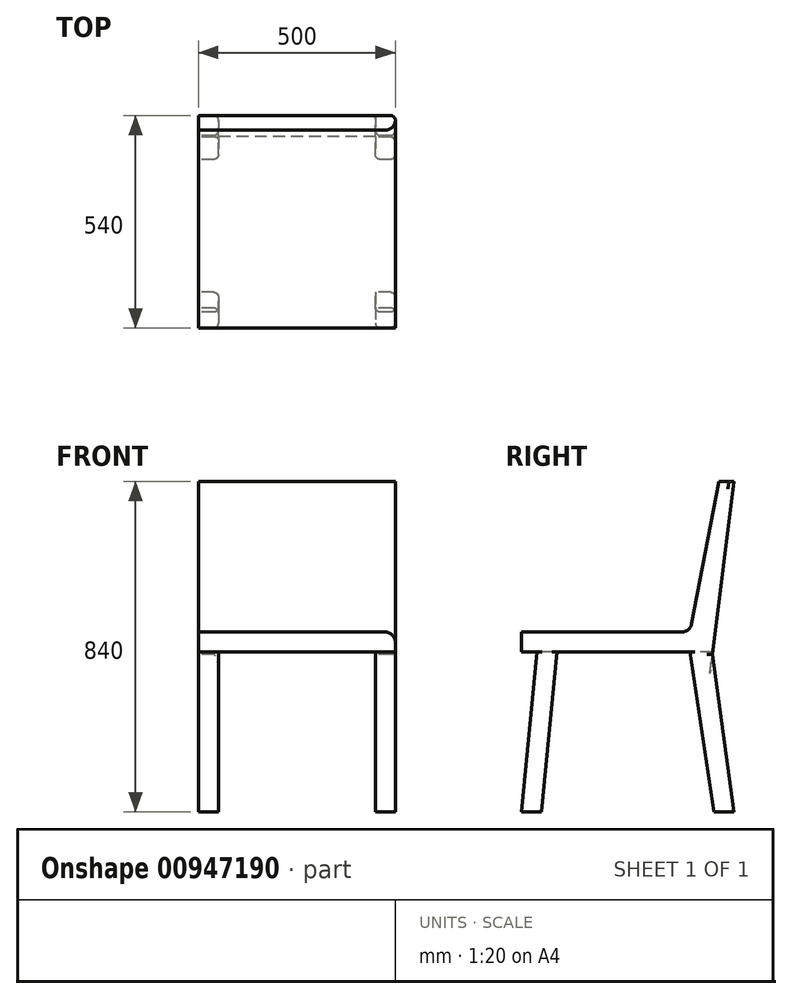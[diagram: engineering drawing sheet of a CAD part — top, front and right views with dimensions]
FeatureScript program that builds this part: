
annotation { "Feature Type Name" : "Feature", "Feature Type Description" : "" }
export const myFeature = defineFeature(function(context is Context, id is Id, definition is map)
    precondition{}
    {
        {
            var Q0;
            Q0=qCreatedBy(makeId("Top.planeOp"),FACE);
            var sketch = newSketch(context, id + "F0", { "sketchPlane" : qUnion([Q0])});
            skLineSegment(sketch, "E0.bottom", {"start": v(0, 0) * mm, "end": v(500, 0) * mm});
            skLineSegment(sketch, "E0.top", {"start": v(0, 540) * mm, "end": v(500, 540) * mm});
            skLineSegment(sketch, "E0.left", {"start": v(0, 0) * mm, "end": v(0, 540) * mm});
            skLineSegment(sketch, "E0.right", {"start": v(500, 0) * mm, "end": v(500, 540) * mm});
            skSolve(sketch);
        }
        {
            var Q0;
            Q0=makeQuery(id+"F0.imprint","IMPRINT",FACE,{"disambiguationData":[TD([[makeQuery(id+"F0.imprint","IMPRINT",EDGE,{"derivedFrom":sQuery(id+"F0.wireOp",EDGE,"E0.bottom")}),1.0]])]});
            extrude(context, id + "F1", {"entities" : qUnion([Q0]), "depth" : 840 * mm, "offsetDistance" : 25.4 * mm});
        }
        {
            var Q0;
            Q0=makeQuery(id+"F1.opExtrude","SWEPT_FACE",FACE,{"disambiguationData":[OSD([sQuery(id+"F0.wireOp",EDGE,"E0.bottom")])]});
            var sketch = newSketch(context, id + "F2", { "sketchPlane" : qUnion([Q0])});
            skLineSegment(sketch, "E1.bottom", {"start": v(50.8, 0) * mm, "end": v(449.2, 0) * mm});
            skLineSegment(sketch, "E1.top", {"start": v(50.8, 406.4) * mm, "end": v(449.2, 406.4) * mm});
            skLineSegment(sketch, "E1.left", {"start": v(50.8, 0) * mm, "end": v(50.8, 406.4) * mm});
            skLineSegment(sketch, "E1.right", {"start": v(449.2, 0) * mm, "end": v(449.2, 406.4) * mm});
            skPoint(sketch, "E2.right.end.orphan", {"position": v(500, 420) * mm});
            skSolve(sketch);
        }
        {
            var Q0;
            Q0 = qSketchRegion(id + "F2", true);
            extrude(context, id + "F3", {"entities" : qUnion([Q0]), "operationType" : NewBodyOperationType.REMOVE, "oppositeDirection" : true, "depth" : 820.42 * mm, "offsetDistance" : 25.4 * mm});
        }
        {
            var Q0;
            Q0=makeQuery(id+"F1.opExtrude","SWEPT_FACE",FACE,{"disambiguationData":[OSD([sQuery(id+"F0.wireOp",EDGE,"E0.left")])]});
            var sketch = newSketch(context, id + "F4", { "sketchPlane" : qUnion([Q0])});
            skLineSegment(sketch, "E3", {"start": v(-489.2, 0) * mm, "end": v(-428.28, 406.4) * mm});
            skLineSegment(sketch, "E4", {"start": v(-428.28, 406.4) * mm, "end": v(-90.89, 406.4) * mm});
            skLineSegment(sketch, "E5", {"start": v(-90.89, 406.4) * mm, "end": v(-50.8, 0) * mm});
            skLineSegment(sketch, "E6", {"start": v(-502.68, 840) * mm, "end": v(-428.28, 457.2) * mm});
            skLineSegment(sketch, "E7", {"start": v(-428.28, 457.2) * mm, "end": v(0, 457.2) * mm});
            skPoint(sketch, "E7.endSnap0", {"position": v(0, 420) * mm});
            skLineSegment(sketch, "E8", {"start": v(0, 457.2) * mm, "end": v(0, 840) * mm});
            skLineSegment(sketch, "E9", {"start": v(-489.2, 0) * mm, "end": v(-50.8, 0) * mm});
            skLineSegment(sketch, "E10.bottom", {"start": v(-540, 840) * mm, "end": v(0, 840) * mm});
            skLineSegment(sketch, "E10.top", {"start": v(-540, 0) * mm, "end": v(0, 0) * mm});
            skLineSegment(sketch, "E10.left", {"start": v(-540, 840) * mm, "end": v(-540, 0) * mm});
            skLineSegment(sketch, "E10.right", {"start": v(0, 840) * mm, "end": v(0, 0) * mm});
            skLineSegment(sketch, "E11", {"start": v(0, 0) * mm, "end": v(-40.09, 406.4) * mm});
            skLineSegment(sketch, "E12", {"start": v(-40.09, 406.4) * mm, "end": v(0, 406.4) * mm});
            skLineSegment(sketch, "E13", {"start": v(-540, 0) * mm, "end": v(-485.04, 400.62) * mm});
            skLineSegment(sketch, "E14", {"start": v(-485.04, 400.62) * mm, "end": v(-540, 840) * mm});
            skSolve(sketch);
        }
        {
            var Q0;
            Q0=makeQuery(id+"F4.imprint","IMPRINT",FACE,{"disambiguationData":[TD([[makeQuery(id+"F4.imprint","IMPRINT",EDGE,{"derivedFrom":sQuery(id+"F4.wireOp",EDGE,"E3")}),-1.0]])]});
            var Q1;
            {var subQ0=sQuery(id+"F4.wireOp",EDGE,"E6");Q1=makeQuery(id+"F4.imprint","IMPRINT",FACE,{"disambiguationData":[TD([[makeQuery(id+"F4.imprint","IMPRINT",EDGE,{"derivedFrom":subQ0}),1.0]])]});}
            var Q2;
            Q2=makeQuery(id+"F4.imprint","IMPRINT",FACE,{"disambiguationData":[TD([[makeQuery(id+"F4.imprint","IMPRINT",EDGE,{"derivedFrom":sQuery(id+"F4.wireOp",EDGE,"E10.left")}),1.0]])]});
            var Q3;
            {var subQ0=sQuery(id+"F4.wireOp",EDGE,"E11");Q3=makeQuery(id+"F4.imprint","IMPRINT",FACE,{"disambiguationData":[TD([[makeQuery(id+"F4.imprint","IMPRINT",EDGE,{"derivedFrom":subQ0}),-1.0]])]});}
            extrude(context, id + "F5", {"entities" : qUnion([Q0, Q1, Q2, Q3]), "operationType" : NewBodyOperationType.REMOVE, "oppositeDirection" : true, "depth" : 772.16 * mm, "offsetDistance" : 25.4 * mm});
        }
        {
            var Q0;
            Q0=makeQuery(id+"F5.boolean.opBoolean","COPY",EDGE,{"derivedFrom":makeQuery(id+"F5.opExtrude","SWEPT_EDGE",EDGE,{"disambiguationData":[OSD([sQuery(id+"F4.wireOp",EDGE,"E6"),sQuery(id+"F4.wireOp",EDGE,"E10.bottom")])]})});
            var Q1;
            Q1=makeQuery(id+"F5.boolean.opBoolean","INTERSECT",EDGE,{"derivedFrom":[makeQuery(id+"F1.opExtrude","SWEPT_FACE",FACE,{"disambiguationData":[OSD([sQuery(id+"F0.wireOp",EDGE,"E0.right")])]}),makeQuery(id+"F5.opExtrude","SWEPT_FACE",FACE,{"disambiguationData":[OSD([sQuery(id+"F4.wireOp",EDGE,"E6")])]})]});
            var Q2;
            Q2=makeQuery(id+"F5.boolean.opBoolean","COPY",EDGE,{"derivedFrom":makeQuery(id+"F5.opExtrude","CAP_EDGE",EDGE,{"disambiguationData":[OSD([sQuery(id+"F4.wireOp",EDGE,"E6")])],"isStart":true})});
            var Q3;
            Q3=makeQuery(id+"F5.boolean.opBoolean","COPY",EDGE,{"derivedFrom":makeQuery(id+"F5.opExtrude","SWEPT_EDGE",EDGE,{"disambiguationData":[OSD([sQuery(id+"F4.wireOp",EDGE,"E6"),sQuery(id+"F4.wireOp",EDGE,"E7")])]})});
            var Q4;
            Q4=makeQuery(id+"F5.boolean.opBoolean","COPY",EDGE,{"derivedFrom":makeQuery(id+"F5.opExtrude","CAP_EDGE",EDGE,{"disambiguationData":[OSD([sQuery(id+"F4.wireOp",EDGE,"E7")])],"isStart":true})});
            var Q5;
            Q5=makeQuery(id+"F5.boolean.opBoolean","INTERSECT",EDGE,{"derivedFrom":[makeQuery(id+"F1.opExtrude","SWEPT_FACE",FACE,{"disambiguationData":[OSD([sQuery(id+"F0.wireOp",EDGE,"E0.right")])]}),makeQuery(id+"F5.opExtrude","SWEPT_FACE",FACE,{"disambiguationData":[OSD([sQuery(id+"F4.wireOp",EDGE,"E7")])]})]});
            var Q6;
            Q6=makeQuery(id+"F5.boolean.opBoolean","COPY",EDGE,{"derivedFrom":makeQuery(id+"F5.opExtrude","SWEPT_EDGE",EDGE,{"disambiguationData":[OSD([sQuery(id+"F4.wireOp",EDGE,"E7"),sQuery(id+"F4.wireOp",EDGE,"E8"),sQuery(id+"F4.wireOp",EDGE,"E10.right")])]})});
            fillet(context, id + "F6", {"entities" : qUnion([Q0, Q1, Q2, Q3, Q4, Q5, Q6]), "radius" : 25.4 * mm, "tangentPropagation" : true, "allowEdgeOverflow" : false});
        }
        {
            var Q0;
            Q0=makeQuery(id+"F5.boolean.opBoolean","INTERSECT",EDGE,{"derivedFrom":[makeQuery(id+"F1.opExtrude","SWEPT_FACE",FACE,{"disambiguationData":[OSD([sQuery(id+"F0.wireOp",EDGE,"E0.right")])]}),makeQuery(id+"F5.opExtrude","SWEPT_FACE",FACE,{"disambiguationData":[OSD([sQuery(id+"F4.wireOp",EDGE,"E11")])]})]});
            var Q1;
            Q1=makeQuery(id+"F5.boolean.opBoolean","INTERSECT",EDGE,{"derivedFrom":[makeQuery(id+"F3.boolean.opBoolean","COPY",FACE,{"derivedFrom":makeQuery(id+"F3.opExtrude","SWEPT_FACE",FACE,{"disambiguationData":[OSD([sQuery(id+"F2.wireOp",EDGE,"E1.right")])]})}),makeQuery(id+"F5.opExtrude","SWEPT_FACE",FACE,{"disambiguationData":[OSD([sQuery(id+"F4.wireOp",EDGE,"E11")])]})]});
            var Q2;
            Q2=makeQuery(id+"F5.boolean.opBoolean","INTERSECT",EDGE,{"derivedFrom":[makeQuery(id+"F1.opExtrude","SWEPT_FACE",FACE,{"disambiguationData":[OSD([sQuery(id+"F0.wireOp",EDGE,"E0.right")])]}),makeQuery(id+"F5.opExtrude","SWEPT_FACE",FACE,{"disambiguationData":[OSD([sQuery(id+"F4.wireOp",EDGE,"E5")])]})]});
            var Q3;
            Q3=makeQuery(id+"F5.boolean.opBoolean","INTERSECT",EDGE,{"derivedFrom":[makeQuery(id+"F3.boolean.opBoolean","COPY",FACE,{"derivedFrom":makeQuery(id+"F3.opExtrude","SWEPT_FACE",FACE,{"disambiguationData":[OSD([sQuery(id+"F2.wireOp",EDGE,"E1.left")])]})}),makeQuery(id+"F5.opExtrude","SWEPT_FACE",FACE,{"disambiguationData":[OSD([sQuery(id+"F4.wireOp",EDGE,"E13")])]})]});
            var Q4;
            Q4=makeQuery(id+"F5.boolean.opBoolean","INTERSECT",EDGE,{"derivedFrom":[makeQuery(id+"F3.boolean.opBoolean","COPY",FACE,{"derivedFrom":makeQuery(id+"F3.opExtrude","SWEPT_FACE",FACE,{"disambiguationData":[OSD([sQuery(id+"F2.wireOp",EDGE,"E1.left")])]})}),makeQuery(id+"F5.opExtrude","SWEPT_FACE",FACE,{"disambiguationData":[OSD([sQuery(id+"F4.wireOp",EDGE,"E3")])]})]});
            var Q5;
            Q5=makeQuery(id+"F5.boolean.opBoolean","COPY",EDGE,{"derivedFrom":makeQuery(id+"F5.opExtrude","CAP_EDGE",EDGE,{"disambiguationData":[OSD([sQuery(id+"F4.wireOp",EDGE,"E3")])],"isStart":true})});
            var Q6;
            Q6=makeQuery(id+"F5.boolean.opBoolean","INTERSECT",EDGE,{"derivedFrom":[makeQuery(id+"F1.opExtrude","SWEPT_FACE",FACE,{"disambiguationData":[OSD([sQuery(id+"F0.wireOp",EDGE,"E0.right")])]}),makeQuery(id+"F5.opExtrude","SWEPT_FACE",FACE,{"disambiguationData":[OSD([sQuery(id+"F4.wireOp",EDGE,"E3")])]})]});
            var Q7;
            Q7=makeQuery(id+"F5.boolean.opBoolean","INTERSECT",EDGE,{"derivedFrom":[makeQuery(id+"F3.boolean.opBoolean","COPY",FACE,{"derivedFrom":makeQuery(id+"F3.opExtrude","SWEPT_FACE",FACE,{"disambiguationData":[OSD([sQuery(id+"F2.wireOp",EDGE,"E1.right")])]})}),makeQuery(id+"F5.opExtrude","SWEPT_FACE",FACE,{"disambiguationData":[OSD([sQuery(id+"F4.wireOp",EDGE,"E3")])]})]});
            var Q8;
            Q8=makeQuery(id+"F5.boolean.opBoolean","INTERSECT",EDGE,{"derivedFrom":[makeQuery(id+"F1.opExtrude","SWEPT_FACE",FACE,{"disambiguationData":[OSD([sQuery(id+"F0.wireOp",EDGE,"E0.right")])]}),makeQuery(id+"F5.opExtrude","SWEPT_FACE",FACE,{"disambiguationData":[OSD([sQuery(id+"F4.wireOp",EDGE,"E13")])]})]});
            var Q9;
            Q9=makeQuery(id+"F5.boolean.opBoolean","INTERSECT",EDGE,{"derivedFrom":[makeQuery(id+"F1.opExtrude","SWEPT_FACE",FACE,{"disambiguationData":[OSD([sQuery(id+"F0.wireOp",EDGE,"E0.right")])]}),makeQuery(id+"F5.opExtrude","SWEPT_FACE",FACE,{"disambiguationData":[OSD([sQuery(id+"F4.wireOp",EDGE,"E14")])]})]});
            var Q10;
            Q10=makeQuery(id+"F5.boolean.opBoolean","INTERSECT",EDGE,{"derivedFrom":[makeQuery(id+"F3.boolean.opBoolean","COPY",FACE,{"derivedFrom":makeQuery(id+"F3.opExtrude","SWEPT_FACE",FACE,{"disambiguationData":[OSD([sQuery(id+"F2.wireOp",EDGE,"E1.left")])]})}),makeQuery(id+"F5.opExtrude","SWEPT_FACE",FACE,{"disambiguationData":[OSD([sQuery(id+"F4.wireOp",EDGE,"E5")])]})]});
            var Q11;
            Q11=makeQuery(id+"F5.boolean.opBoolean","INTERSECT",EDGE,{"derivedFrom":[makeQuery(id+"F3.boolean.opBoolean","COPY",FACE,{"derivedFrom":makeQuery(id+"F3.opExtrude","SWEPT_FACE",FACE,{"disambiguationData":[OSD([sQuery(id+"F2.wireOp",EDGE,"E1.left")])]})}),makeQuery(id+"F5.opExtrude","SWEPT_FACE",FACE,{"disambiguationData":[OSD([sQuery(id+"F4.wireOp",EDGE,"E11")])]})]});
            var Q12;
            Q12=makeQuery(id+"F5.boolean.opBoolean","COPY",EDGE,{"derivedFrom":makeQuery(id+"F5.opExtrude","CAP_EDGE",EDGE,{"disambiguationData":[OSD([sQuery(id+"F4.wireOp",EDGE,"E11")])],"isStart":true})});
            var Q13;
            Q13=makeQuery(id+"F5.boolean.opBoolean","COPY",EDGE,{"derivedFrom":makeQuery(id+"F5.opExtrude","CAP_EDGE",EDGE,{"disambiguationData":[OSD([sQuery(id+"F4.wireOp",EDGE,"E5")])],"isStart":true})});
            var Q14;
            Q14=makeQuery(id+"F5.boolean.opBoolean","COPY",EDGE,{"derivedFrom":makeQuery(id+"F5.opExtrude","CAP_EDGE",EDGE,{"disambiguationData":[OSD([sQuery(id+"F4.wireOp",EDGE,"E13")])],"isStart":true})});
            fillet(context, id + "F7", {"entities" : qUnion([Q0, Q1, Q2, Q3, Q4, Q5, Q6, Q7, Q8, Q9, Q10, Q11, Q12, Q13, Q14]), "radius" : 12.7 * mm, "tangentPropagation" : true, "allowEdgeOverflow" : false});
        }
    });
